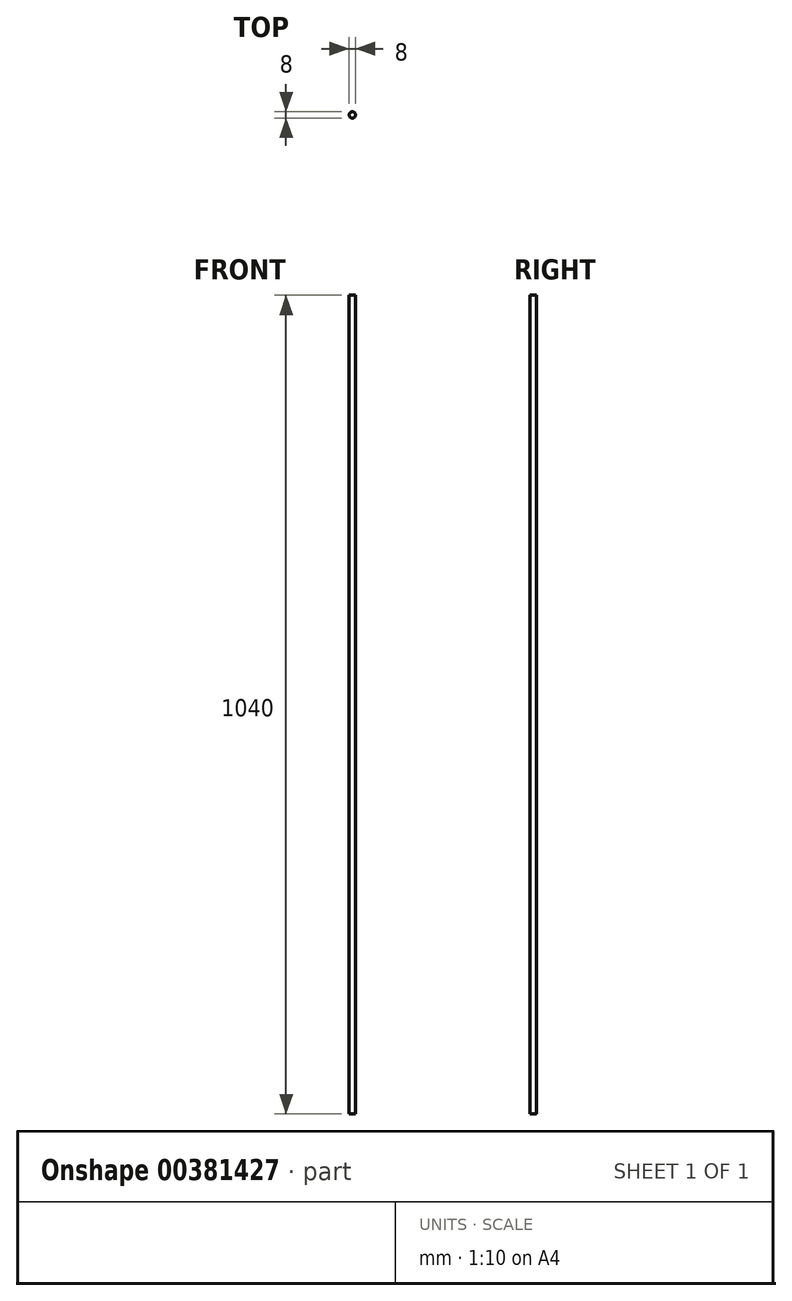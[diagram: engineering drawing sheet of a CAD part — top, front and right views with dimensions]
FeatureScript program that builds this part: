
annotation { "Feature Type Name" : "Feature", "Feature Type Description" : "" }
export const myFeature = defineFeature(function(context is Context, id is Id, definition is map)
    precondition{}
    {
        {
            var Q0;
            Q0=qCreatedBy(makeId("Top.planeOp"),FACE);
            var sketch = newSketch(context, id + "F0", { "sketchPlane" : qUnion([Q0])});
            skCircle(sketch, "E0", {"center": v(0, 0) * mm, "radius": 4 * mm});
            skSolve(sketch);
        }
        {
            var Q0;
            Q0 = qSketchRegion(id + "F0", true);
            extrude(context, id + "F1", {"entities" : qUnion([Q0]), "depth" : 1040 * mm});
        }
    });
